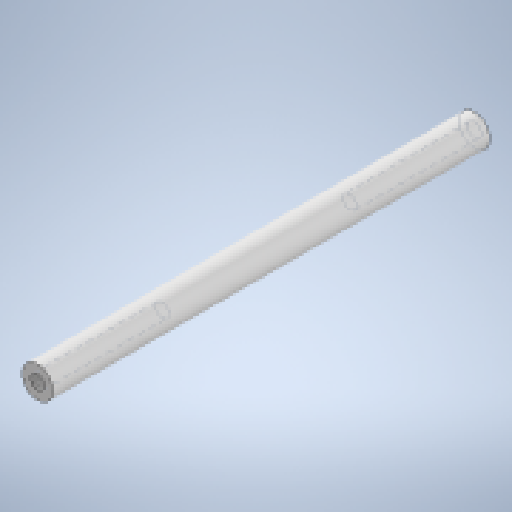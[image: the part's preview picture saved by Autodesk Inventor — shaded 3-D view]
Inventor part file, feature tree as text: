
AUTODESK INVENTOR PART (.ipt)
format: ipt  version: 2023 (Build 270158000, 158)  size: 166,912 bytes
history: native  units: mm
features: extrude x3, sketch x3, thread x2
ambient origin geometry x8: Origin, YZ Plane, XZ Plane, XY Plane, X Axis, Y Axis, Z Axis, Center Point
bodies: Solid1 (feature_tree)
feature tree (8):
  extrude  "Extrusion1"  Depth=70.0mm TaperAngle=0.0deg
  extrude  "Extrusion2"  Depth=20.0mm TaperAngle=0.0deg
  extrude  "Extrusion3"  Depth=20.0mm TaperAngle=0.0deg
  thread  "Thread1"  [1 undecoded]
  thread  "Thread2"  [1 undecoded]
  sketch  "Sketch1"  dims[d0=5.0mm d1=70.0mm d2=0.0mm]
  sketch  "Sketch2"  dims[d3=2.2mm d4=20.0mm d5=0.0mm]
  sketch  "Sketch3"  dims[d6=20.0mm d7=0.0mm d8=16.0mm d9=0.0mm d10=16.0mm d11=0.0mm]
note: 2 required parameter values undecoded (feature->parameter linkage not recoverable at this tier; creation-order binding heuristic only, values carry confidence <= 0.55)
